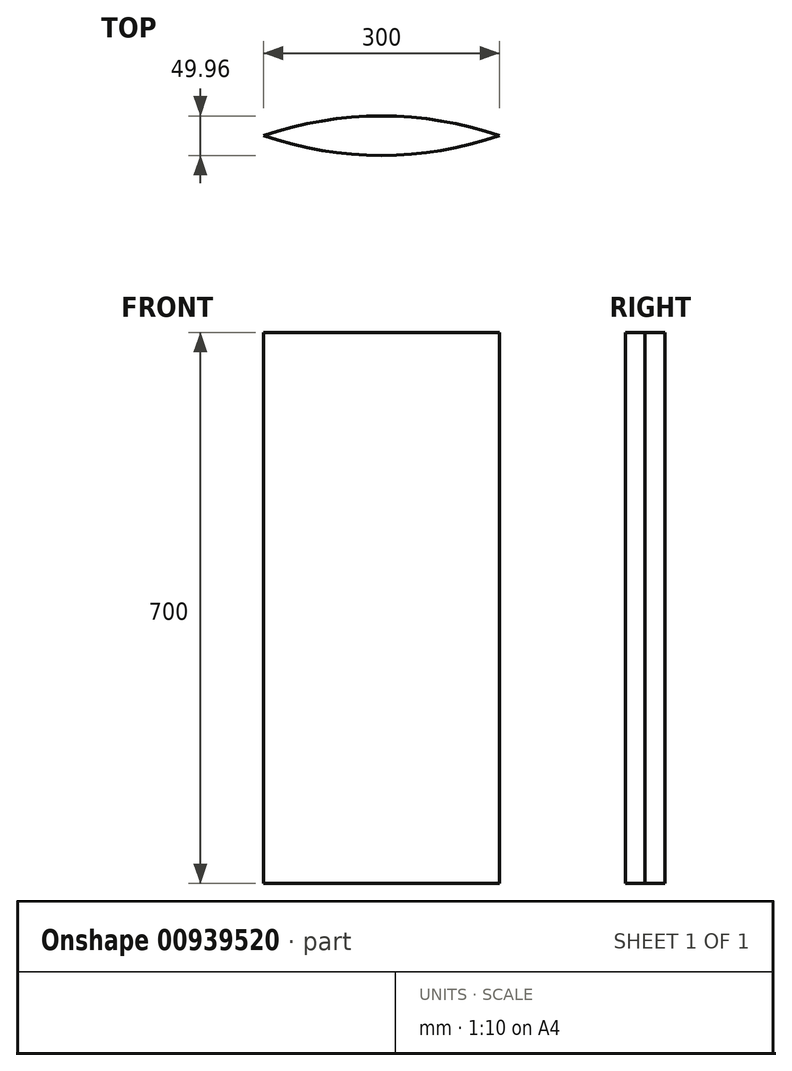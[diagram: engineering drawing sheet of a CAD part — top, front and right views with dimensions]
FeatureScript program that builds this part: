
annotation { "Feature Type Name" : "Feature", "Feature Type Description" : "" }
export const myFeature = defineFeature(function(context is Context, id is Id, definition is map)
    precondition{}
    {
        {
            var Q0;
            Q0=qCreatedBy(makeId("Top.planeOp"),FACE);
            var sketch = newSketch(context, id + "F0", { "sketchPlane" : qUnion([Q0])});
            skArc(sketch, "E0", {"start": v(300, 0) * mm, "mid": v(150, 24.98) * mm, "end": v(0, 0) * mm});
            skLineSegment(sketch, "E1", {"start": v(0, 0) * mm, "end": v(300, 0) * mm});
            skSolve(sketch);
        }
        {
            var Q0;
            Q0=makeQuery(id+"F0.imprint","IMPRINT",FACE,{"disambiguationData":[TD([[makeQuery(id+"F0.imprint","IMPRINT",EDGE,{"derivedFrom":sQuery(id+"F0.wireOp",EDGE,"E0")}),1.0]])]});
            extrude(context, id + "F1", {"entities" : qUnion([Q0]), "oppositeDirection" : true, "depth" : 700 * mm, "offsetDistance" : 25 * mm});
        }
        {
            var Q0;
            Q0=makeQuery(id+"F1.opExtrude","SWEPT_BODY",BODY,{"disambiguationData":[OSD([sQuery(id+"F0.wireOp",EDGE,"E0"),sQuery(id+"F0.wireOp",EDGE,"E1")])]});
            var Q1;
            Q1=qCreatedBy(makeId("Front.planeOp"),FACE);
            mirror(context, id + "F2", {"operationType" : NewBodyOperationType.ADD, "entities" : qUnion([Q0]), "mirrorPlane" : qUnion([Q1])});
        }
    });
